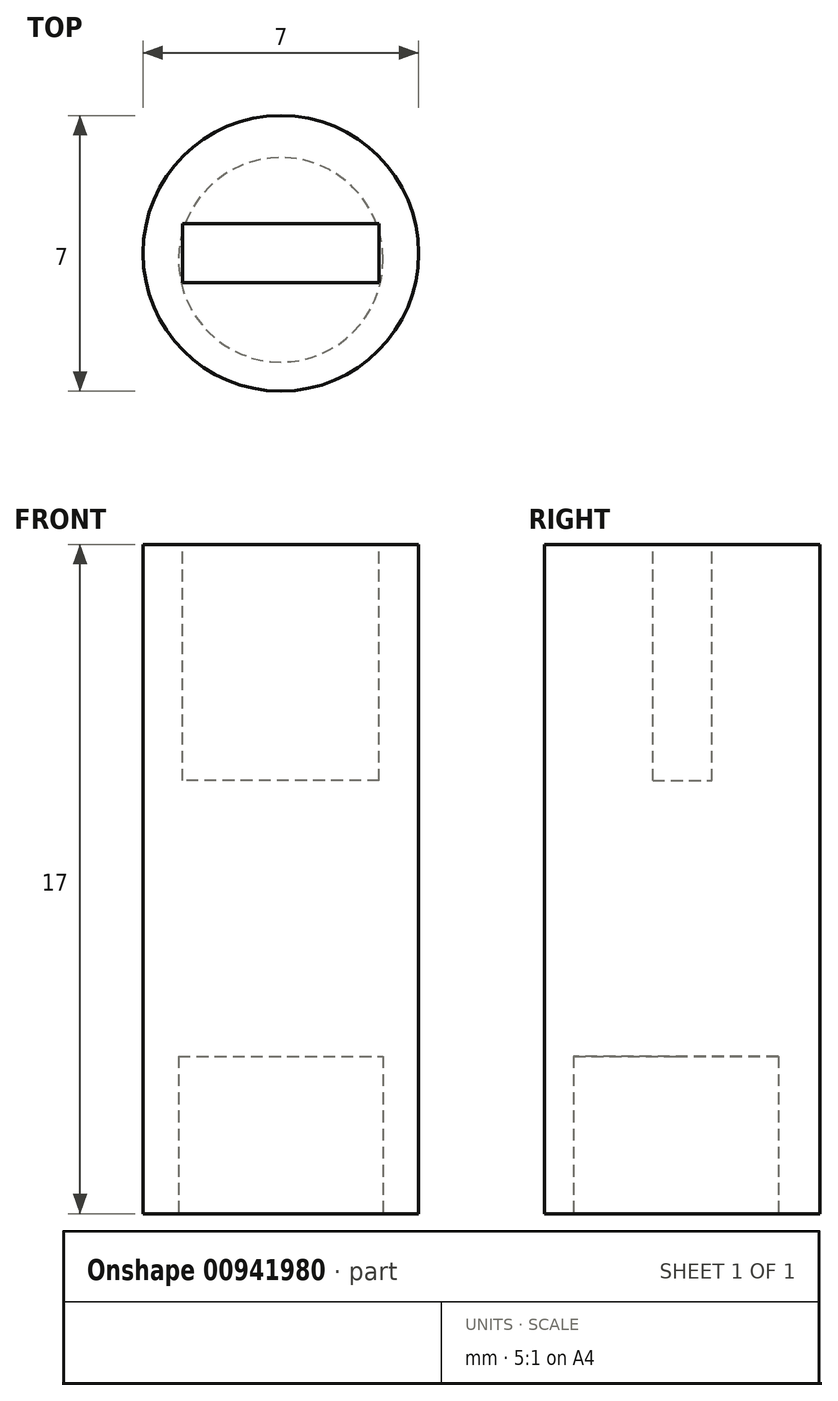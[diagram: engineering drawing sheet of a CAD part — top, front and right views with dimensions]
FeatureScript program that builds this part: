
annotation { "Feature Type Name" : "Feature", "Feature Type Description" : "" }
export const myFeature = defineFeature(function(context is Context, id is Id, definition is map)
    precondition{}
    {
        {
            var Q0;
            Q0=qCreatedBy(makeId("Top.planeOp"),FACE);
            var sketch = newSketch(context, id + "F0", { "sketchPlane" : qUnion([Q0])});
            skCircle(sketch, "E0", {"center": v(0, 0) * mm, "radius": 3.5 * mm});
            skSolve(sketch);
        }
        {
            var Q0;
            Q0 = qSketchRegion(id + "F0", true);
            var Q1;
            Q1=makeQuery(id+"F0.imprint","IMPRINT",FACE,{"disambiguationData":[TD([[makeQuery(id+"F0.imprint","IMPRINT",EDGE,{"derivedFrom":sQuery(id+"F0.wireOp",EDGE,"E0")}),1.0]])]});
            extrude(context, id + "F1", {"entities" : qUnion([Q0, Q1]), "depth" : 10 * mm, "offsetDistance" : 25 * mm});
        }
        {
            var Q0;
            Q0=makeQuery(id+"F1.opExtrude","CAP_FACE",FACE,{"disambiguationData":[OSD([sQuery(id+"F0.wireOp",EDGE,"E0")])],"isStart":true});
            var sketch = newSketch(context, id + "F2", { "sketchPlane" : qUnion([Q0])});
            skCircle(sketch, "E1", {"center": v(0, 0.16) * mm, "radius": 2.6 * mm});
            skSolve(sketch);
        }
        {
            var Q0;
            Q0=makeQuery(id+"F2.imprint","IMPRINT",FACE,{"disambiguationData":[TD([[makeQuery(id+"F2.imprint","IMPRINT",EDGE,{"derivedFrom":sQuery(id+"F2.wireOp",EDGE,"E1")}),1.0]])]});
            extrude(context, id + "F3", {"entities" : qUnion([Q0]), "operationType" : NewBodyOperationType.REMOVE, "oppositeDirection" : true, "depth" : 4 * mm, "offsetDistance" : 25 * mm});
        }
        {
            var Q0;
            Q0=makeQuery(id+"F1.opExtrude","CAP_FACE",FACE,{"disambiguationData":[OSD([sQuery(id+"F0.wireOp",EDGE,"E0")])],"isStart":false});
            extrude(context, id + "F4", {"entities" : qUnion([Q0]), "operationType" : NewBodyOperationType.ADD, "depth" : 7 * mm, "offsetDistance" : 25 * mm});
        }
        {
            var Q0;
            Q0=makeQuery(id+"F4.opExtrude","CAP_FACE",FACE,{"disambiguationData":[OSD([sQuery(id+"F0.wireOp",EDGE,"E0")])],"isStart":false});
            var sketch = newSketch(context, id + "F5", { "sketchPlane" : qUnion([Q0])});
            skLineSegment(sketch, "E2.bottom", {"start": v(2.5, -0.75) * mm, "end": v(-2.5, -0.75) * mm});
            skLineSegment(sketch, "E2.top", {"start": v(2.5, 0.75) * mm, "end": v(-2.5, 0.75) * mm});
            skLineSegment(sketch, "E2.left", {"start": v(2.5, -0.75) * mm, "end": v(2.5, 0.75) * mm});
            skLineSegment(sketch, "E2.right", {"start": v(-2.5, -0.75) * mm, "end": v(-2.5, 0.75) * mm});
            skSolve(sketch);
        }
        {
            var Q0;
            Q0=makeQuery(id+"F5.imprint","IMPRINT",FACE,{"disambiguationData":[TD([[makeQuery(id+"F5.imprint","IMPRINT",EDGE,{"derivedFrom":sQuery(id+"F5.wireOp",EDGE,"E2.bottom")}),-1.0]])]});
            extrude(context, id + "F6", {"entities" : qUnion([Q0]), "operationType" : NewBodyOperationType.REMOVE, "oppositeDirection" : true, "depth" : 6 * mm, "offsetDistance" : 25 * mm});
        }
    });
